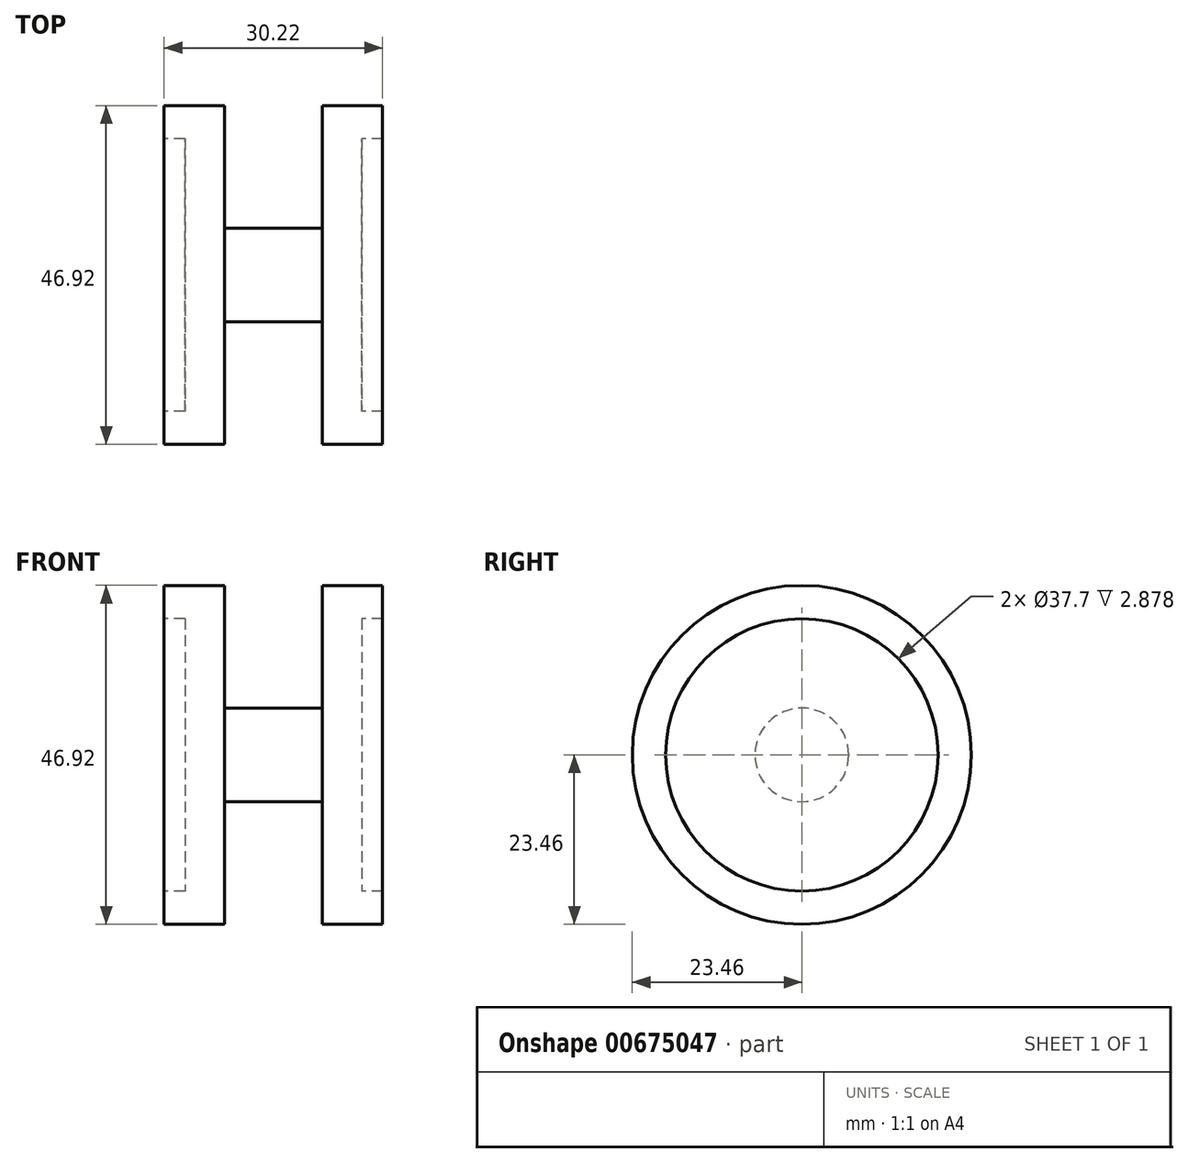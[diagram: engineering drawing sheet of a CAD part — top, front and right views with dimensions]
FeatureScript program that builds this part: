
annotation { "Feature Type Name" : "Feature", "Feature Type Description" : "" }
export const myFeature = defineFeature(function(context is Context, id is Id, definition is map)
    precondition{}
    {
        {
            var Q0;
            Q0=qCreatedBy(makeId("Front.planeOp"),FACE);
            var sketch = newSketch(context, id + "F0", { "sketchPlane" : qUnion([Q0])});
            skLineSegment(sketch, "E0.bottom", {"start": v(0, 0) * mm, "end": v(-6.76, 0) * mm});
            skLineSegment(sketch, "E0.top", {"start": v(0, 6.48) * mm, "end": v(-6.76, 6.48) * mm});
            skLineSegment(sketch, "E0.left", {"start": v(0, 0) * mm, "end": v(0, 6.48) * mm});
            skLineSegment(sketch, "E0.right", {"start": v(-6.76, 0) * mm, "end": v(-6.76, 6.48) * mm});
            skLineSegment(sketch, "E1.bottom", {"start": v(-6.76, 0) * mm, "end": v(-12.23, 0) * mm});
            skLineSegment(sketch, "E1.top", {"start": v(-6.76, 23.46) * mm, "end": v(-12.23, 23.46) * mm});
            skLineSegment(sketch, "E1.left", {"start": v(-6.76, 0) * mm, "end": v(-6.76, 23.46) * mm});
            skLineSegment(sketch, "E1.right", {"start": v(-12.23, 0) * mm, "end": v(-12.23, 23.46) * mm});
            skLineSegment(sketch, "E2.bottom", {"start": v(-12.23, 23.46) * mm, "end": v(-15.1, 23.46) * mm});
            skLineSegment(sketch, "E2.top", {"start": v(-12.23, 18.85) * mm, "end": v(-15.1, 18.85) * mm});
            skLineSegment(sketch, "E2.left", {"start": v(-12.23, 23.46) * mm, "end": v(-12.23, 18.85) * mm});
            skLineSegment(sketch, "E2.right", {"start": v(-15.1, 23.46) * mm, "end": v(-15.1, 18.85) * mm});
            skLineSegment(sketch, "E3.MirrorCS", {"start": v(0, 6.48) * mm, "end": v(6.76, 6.48) * mm});
            skLineSegment(sketch, "E4.MirrorCS", {"start": v(0, 0) * mm, "end": v(6.76, 0) * mm});
            skLineSegment(sketch, "E5.MirrorCS", {"start": v(6.76, 0) * mm, "end": v(12.23, 0) * mm});
            skLineSegment(sketch, "E6.MirrorCS", {"start": v(12.23, 0) * mm, "end": v(12.23, 23.46) * mm});
            skLineSegment(sketch, "E7.MirrorCS", {"start": v(6.76, 0) * mm, "end": v(6.76, 23.46) * mm});
            skLineSegment(sketch, "E8.MirrorCS", {"start": v(6.76, 23.46) * mm, "end": v(12.23, 23.46) * mm});
            skLineSegment(sketch, "E9.MirrorCS", {"start": v(12.23, 18.85) * mm, "end": v(15.1, 18.85) * mm});
            skLineSegment(sketch, "E10.MirrorCS", {"start": v(15.1, 23.46) * mm, "end": v(15.1, 18.85) * mm});
            skLineSegment(sketch, "E11.MirrorCS", {"start": v(12.23, 23.46) * mm, "end": v(15.1, 23.46) * mm});
            skLineSegment(sketch, "E12", {"start": v(-23.76, 0) * mm, "end": v(32.32, 0) * mm, "construction": true});
            skPoint(sketch, "E12.endSnap0", {"position": v(9.5, 0) * mm});
            skSolve(sketch);
        }
        {
            var Q0;
            {var subQ3=sQuery(id+"F0.wireOp",EDGE,"E1.bottom");Q0=makeQuery(id+"F0.imprint","IMPRINT",FACE,{"disambiguationData":[TD([[makeQuery(id+"F0.imprint","IMPRINT",EDGE,{"derivedFrom":subQ3}),-1.0]])]});}
            var Q1;
            Q1=makeQuery(id+"F0.imprint","IMPRINT",FACE,{"disambiguationData":[TD([[makeQuery(id+"F0.imprint","IMPRINT",EDGE,{"derivedFrom":sQuery(id+"F0.wireOp",EDGE,"E2.bottom")}),1.0]])]});
            var Q2;
            {var subQ0=sQuery(id+"F0.wireOp",EDGE,"E0.bottom");Q2=makeQuery(id+"F0.imprint","IMPRINT",FACE,{"disambiguationData":[TD([[makeQuery(id+"F0.imprint","IMPRINT",EDGE,{"derivedFrom":subQ0}),-1.0]])]});}
            var Q3;
            Q3=makeQuery(id+"F0.imprint","IMPRINT",FACE,{"disambiguationData":[TD([[makeQuery(id+"F0.imprint","IMPRINT",EDGE,{"derivedFrom":sQuery(id+"F0.wireOp",EDGE,"E0.left")}),-1.0]])]});
            var Q4;
            {var subQ2=sQuery(id+"F0.wireOp",EDGE,"E5.MirrorCS");Q4=makeQuery(id+"F0.imprint","IMPRINT",FACE,{"disambiguationData":[TD([[makeQuery(id+"F0.imprint","IMPRINT",EDGE,{"derivedFrom":subQ2}),1.0]])]});}
            var Q5;
            {var subQ2=sQuery(id+"F0.wireOp",EDGE,"E9.MirrorCS");Q5=makeQuery(id+"F0.imprint","IMPRINT",FACE,{"disambiguationData":[TD([[makeQuery(id+"F0.imprint","IMPRINT",EDGE,{"derivedFrom":subQ2}),1.0]])]});}
            var Q6;
            Q6=sQuery(id+"F0.wireOp",EDGE,"E12");
            revolve(context, id + "F1", {"entities" : qUnion([Q0, Q1, Q2, Q3, Q4, Q5]), "axis" : qUnion([Q6]), "revolveType" : RevolveType.FULL});
        }
    });
